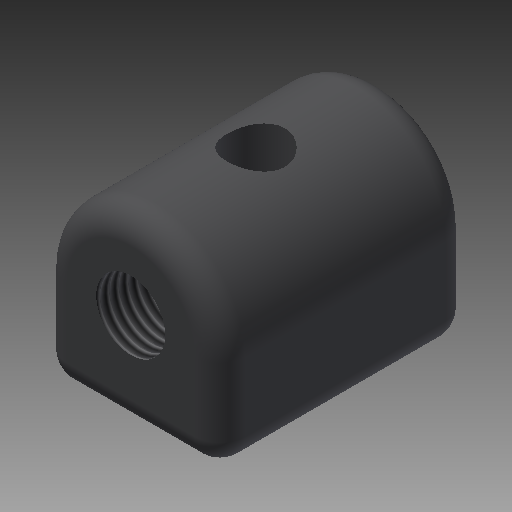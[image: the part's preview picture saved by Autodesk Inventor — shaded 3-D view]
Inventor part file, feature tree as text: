
AUTODESK INVENTOR PART (.ipt)
format: ipt  version: 2019 (Build 230136000, 136)  size: 219,648 bytes
history: native  units: mm
features: extrude x4, sketch x4, fillet x2, thread x1
ambient origin geometry x8: Origin, YZ Plane, XZ Plane, XY Plane, X Axis, Y Axis, Z Axis, Center Point
bodies: Solid1 (feature_tree)
feature tree (11):
  extrude  "Extrusion1"  Depth=14.25mm
  fillet  "Fillet1"  Radius=14.25mm
  extrude  "Extrusion2"  Depth=4.0mm
  fillet  "Fillet2"  Radius=9.2mm
  extrude  "Extrusion3"  Depth=4.0mm
  extrude  "Extrusion4"  Depth=10.0mm
  thread  "Thread1"  [1 undecoded]
  sketch  "Sketch1"  dims[d0=28.5mm d1=14.25mm d3=14.25mm]
  sketch  "Sketch2"  dims[d6=40.0mm d7=0.0mm d8=4.0mm d9=9.2mm]
  sketch  "Sketch3"  dims[d10=39.4mm d11=0.0mm d12=4.0mm]
  sketch  "Sketch4"  dims[d13=1.5mm d14=0.0mm d16=15.0mm d17=17.175mm d18=11.0mm d19=10.0mm d20=0.0mm d21=10.0mm d22=0.0mm]
note: 1 required parameter value undecoded (feature->parameter linkage not recoverable at this tier; creation-order binding heuristic only, values carry confidence <= 0.55)
